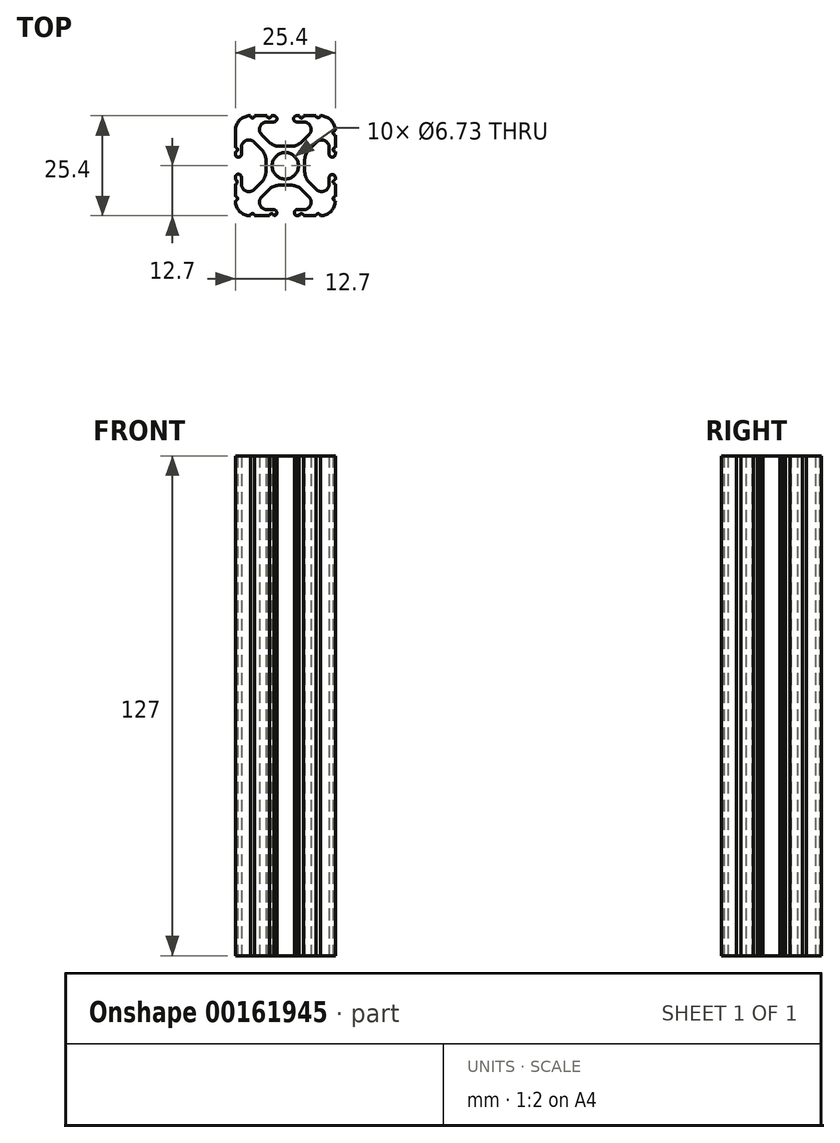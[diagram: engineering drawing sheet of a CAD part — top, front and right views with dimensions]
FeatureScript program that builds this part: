
annotation { "Feature Type Name" : "Feature", "Feature Type Description" : "" }
export const myFeature = defineFeature(function(context is Context, id is Id, definition is map)
    precondition{}
    {
        {
            var Q0;
            Q0=qCreatedBy(makeId("Top.planeOp"),FACE);
            var sketch = newSketch(context, id + "F0", { "sketchPlane" : qUnion([Q0])});
            skCircle(sketch, "E0", {"center": v(-12.7, 12.7) * mm, "radius": 3.36 * mm});
            skLineSegment(sketch, "E1.bottom", {"start": v(-11.24, 17.64) * mm, "end": v(-14.16, 17.64) * mm});
            skLineSegment(sketch, "E1.top", {"start": v(-11.24, 7.76) * mm, "end": v(-14.16, 7.76) * mm});
            skLineSegment(sketch, "E1.left", {"start": v(-7.76, 14.16) * mm, "end": v(-7.76, 11.24) * mm});
            skLineSegment(sketch, "E1.right", {"start": v(-17.64, 14.16) * mm, "end": v(-17.64, 11.24) * mm});
            skPoint(sketch, "E2.visualSharp", {"position": v(-25.4, 25.4) * mm});
            skPoint(sketch, "E3.visualSharp", {"position": v(0, 25.4) * mm});
            skPoint(sketch, "E4.visualSharp", {"position": v(0, 0) * mm});
            skPoint(sketch, "E5.visualSharp", {"position": v(-25.4, 0) * mm});
            skLineSegment(sketch, "E6.0", {"start": v(-18.7, 20.6) * mm, "end": v(-16.85, 18.76) * mm});
            skLineSegment(sketch, "E7.0", {"start": v(-20.6, 18.7) * mm, "end": v(-18.76, 16.85) * mm});
            skPoint(sketch, "E8.orphan", {"position": v(-23.85, 1.55) * mm});
            skPoint(sketch, "E9.orphan", {"position": v(-23.85, 23.85) * mm});
            skPoint(sketch, "E10.orphan", {"position": v(-1.55, 23.85) * mm});
            skPoint(sketch, "E11.orphan", {"position": v(-1.55, 1.55) * mm});
            skLineSegment(sketch, "E12", {"start": v(-8.55, 6.64) * mm, "end": v(-6.7, 4.8) * mm});
            skLineSegment(sketch, "E13.0", {"start": v(-18.7, 4.8) * mm, "end": v(-16.85, 6.64) * mm});
            skLineSegment(sketch, "E14.0", {"start": v(-20.6, 6.7) * mm, "end": v(-18.76, 8.55) * mm});
            skLineSegment(sketch, "E15.0", {"start": v(-8.55, 18.76) * mm, "end": v(-6.7, 20.6) * mm});
            skPoint(sketch, "E16.visualSharp", {"position": v(-23.85, 21.95) * mm});
            skArc(sketch, "E16.filletArc", {"start": v(-20.6, 18.7) * mm, "mid": v(-22.68, 19.1) * mm, "end": v(-23.85, 17.35) * mm});
            skPoint(sketch, "E17.visualSharp", {"position": v(-21.95, 23.85) * mm});
            skArc(sketch, "E17.filletArc", {"start": v(-17.35, 23.85) * mm, "mid": v(-19.1, 22.68) * mm, "end": v(-18.7, 20.6) * mm});
            skPoint(sketch, "E18.visualSharp", {"position": v(-5.34, 23.85) * mm});
            skLineSegment(sketch, "E19", {"start": v(-17.35, 23.85) * mm, "end": v(-15.58, 23.85) * mm});
            skLineSegment(sketch, "E20", {"start": v(-23.85, 17.35) * mm, "end": v(-23.85, 15.62) * mm});
            skLineSegment(sketch, "E21", {"start": v(-8.05, 1.55) * mm, "end": v(-9.78, 1.55) * mm});
            skArc(sketch, "E22.filletArc", {"start": v(-6.7, 20.6) * mm, "mid": v(-6.3, 22.68) * mm, "end": v(-8.05, 23.85) * mm});
            skPoint(sketch, "E23.visualSharp", {"position": v(-1.55, 3.45) * mm});
            skPoint(sketch, "E24.visualSharp", {"position": v(-3.45, 1.55) * mm});
            skArc(sketch, "E24.filletArc", {"start": v(-8.05, 1.55) * mm, "mid": v(-6.3, 2.73) * mm, "end": v(-6.7, 4.8) * mm});
            skArc(sketch, "E25.filletArc", {"start": v(-18.7, 4.8) * mm, "mid": v(-19.1, 2.73) * mm, "end": v(-17.35, 1.55) * mm});
            skArc(sketch, "E26.filletArc", {"start": v(-23.85, 8.05) * mm, "mid": v(-22.68, 6.3) * mm, "end": v(-20.6, 6.7) * mm});
            skLineSegment(sketch, "E27.bottom", {"start": v(-4.9, 0) * mm, "end": v(-8.05, 0) * mm});
            skLineSegment(sketch, "E27.top", {"start": v(-4.92, 25.4) * mm, "end": v(-8.05, 25.4) * mm});
            skLineSegment(sketch, "E27.left", {"start": v(0, 4.9) * mm, "end": v(0, 8.05) * mm});
            skLineSegment(sketch, "E27.right", {"start": v(-25.4, 4.9) * mm, "end": v(-25.4, 8.05) * mm});
            skArc(sketch, "E28.filletArc", {"start": v(-25.4, 3.81) * mm, "mid": v(-24.28, 1.12) * mm, "end": v(-21.59, 0) * mm});
            skArc(sketch, "E29.filletArc", {"start": v(-3.81, 0) * mm, "mid": v(-1.12, 1.12) * mm, "end": v(0, 3.8) * mm});
            skArc(sketch, "E30.filletArc", {"start": v(0, 21.59) * mm, "mid": v(-1.12, 24.28) * mm, "end": v(-3.8, 25.4) * mm});
            skArc(sketch, "E31.filletArc", {"start": v(-21.59, 25.4) * mm, "mid": v(-24.28, 24.28) * mm, "end": v(-25.4, 21.59) * mm});
            skPoint(sketch, "E32.newPointA", {"position": v(-17.64, 7.76) * mm});
            skArc(sketch, "E32.filletArc", {"start": v(-14.16, 7.76) * mm, "mid": v(-15.62, 7.47) * mm, "end": v(-16.85, 6.64) * mm});
            skPoint(sketch, "E33.newPointA", {"position": v(-7.76, 7.76) * mm});
            skArc(sketch, "E33.filletArc", {"start": v(-8.55, 6.64) * mm, "mid": v(-9.78, 7.47) * mm, "end": v(-11.24, 7.76) * mm});
            skArc(sketch, "E34.filletArc", {"start": v(-7.76, 11.24) * mm, "mid": v(-7.47, 9.78) * mm, "end": v(-6.64, 8.55) * mm});
            skArc(sketch, "E35.filletArc", {"start": v(-6.64, 16.85) * mm, "mid": v(-7.47, 15.62) * mm, "end": v(-7.76, 14.16) * mm});
            skPoint(sketch, "E36.newPointB", {"position": v(-7.76, 17.64) * mm});
            skArc(sketch, "E36.filletArc", {"start": v(-11.24, 17.64) * mm, "mid": v(-9.78, 17.93) * mm, "end": v(-8.55, 18.76) * mm});
            skPoint(sketch, "E37.newPointB", {"position": v(-17.64, 17.64) * mm});
            skArc(sketch, "E37.filletArc", {"start": v(-16.85, 18.76) * mm, "mid": v(-15.62, 17.93) * mm, "end": v(-14.16, 17.64) * mm});
            skArc(sketch, "E38.filletArc", {"start": v(-17.64, 14.16) * mm, "mid": v(-17.93, 15.62) * mm, "end": v(-18.76, 16.85) * mm});
            skArc(sketch, "E39.filletArc", {"start": v(-18.76, 8.55) * mm, "mid": v(-17.93, 9.78) * mm, "end": v(-17.64, 11.24) * mm});
            skLineSegment(sketch, "E40", {"start": v(-6.64, 8.55) * mm, "end": v(-4.8, 6.7) * mm});
            skPoint(sketch, "E41.visualSharp", {"position": v(-1.55, 21.95) * mm});
            skArc(sketch, "E42.filletArc", {"start": v(-4.8, 6.7) * mm, "mid": v(-2.73, 6.3) * mm, "end": v(-1.55, 8.05) * mm});
            skLineSegment(sketch, "E43", {"start": v(-1.55, 8.05) * mm, "end": v(-1.55, 9.78) * mm});
            skLineSegment(sketch, "E44", {"start": v(-6.64, 16.85) * mm, "end": v(-4.8, 18.7) * mm});
            skArc(sketch, "E45.filletArc", {"start": v(-1.55, 17.35) * mm, "mid": v(-2.73, 19.1) * mm, "end": v(-4.8, 18.7) * mm});
            skArc(sketch, "E46", {"start": v(-23.85, 9.78) * mm, "mid": v(-24.63, 10.56) * mm, "end": v(-25.4, 9.78) * mm});
            skArc(sketch, "E47", {"start": v(-25.4, 15.62) * mm, "mid": v(-24.63, 14.86) * mm, "end": v(-23.85, 15.62) * mm});
            skArc(sketch, "E48", {"start": v(-15.62, 23.85) * mm, "mid": v(-14.83, 24.63) * mm, "end": v(-15.62, 25.4) * mm});
            skArc(sketch, "E49", {"start": v(-9.78, 25.4) * mm, "mid": v(-10.6, 24.63) * mm, "end": v(-9.78, 23.85) * mm});
            skArc(sketch, "E50", {"start": v(-1.55, 15.62) * mm, "mid": v(-0.77, 14.88) * mm, "end": v(0, 15.62) * mm});
            skArc(sketch, "E51", {"start": v(0, 9.78) * mm, "mid": v(-0.77, 10.5) * mm, "end": v(-1.55, 9.78) * mm});
            skArc(sketch, "E52", {"start": v(-9.78, 1.55) * mm, "mid": v(-10.4, 0.77) * mm, "end": v(-9.78, 0) * mm});
            skArc(sketch, "E53", {"start": v(-15.62, 0) * mm, "mid": v(-14.85, 0.77) * mm, "end": v(-15.62, 1.55) * mm});
            skLineSegment(sketch, "E54.trimOffspring", {"start": v(-15.62, 1.55) * mm, "end": v(-17.35, 1.55) * mm});
            skLineSegment(sketch, "E55.trimOffspring", {"start": v(-16.7, 0) * mm, "end": v(-20.5, 0) * mm});
            skLineSegment(sketch, "E56.trimOffspring", {"start": v(-1.55, 15.62) * mm, "end": v(-1.55, 17.35) * mm});
            skLineSegment(sketch, "E57.trimOffspring", {"start": v(0, 15.62) * mm, "end": v(0, 16.26) * mm});
            skLineSegment(sketch, "E58.trimOffspring", {"start": v(-23.85, 9.78) * mm, "end": v(-23.85, 8.05) * mm});
            skLineSegment(sketch, "E59.trimOffspring", {"start": v(-25.4, 15.62) * mm, "end": v(-25.4, 16.26) * mm});
            skLineSegment(sketch, "E60.trimOffspring", {"start": v(-9.86, 23.85) * mm, "end": v(-8.05, 23.85) * mm});
            skLineSegment(sketch, "E61.trimOffspring", {"start": v(-15.58, 25.4) * mm, "end": v(-16.25, 25.4) * mm});
            skPoint(sketch, "E62.start.orphan", {"position": v(-15.62, 17.93) * mm});
            skPoint(sketch, "E63.start.orphan", {"position": v(-9.78, 17.93) * mm});
            skPoint(sketch, "E64.start.orphan", {"position": v(-7.47, 15.62) * mm});
            skPoint(sketch, "E65.start.orphan", {"position": v(-7.47, 9.78) * mm});
            skPoint(sketch, "E66.start.orphan", {"position": v(-17.93, 15.62) * mm});
            skPoint(sketch, "E67.start.orphan", {"position": v(-17.93, 9.78) * mm});
            skPoint(sketch, "E68.start.orphan", {"position": v(-9.78, 7.47) * mm});
            skPoint(sketch, "E69.start.orphan", {"position": v(-15.62, 7.47) * mm});
            skPoint(sketch, "E70.endSnap0", {"position": v(0, 18.6) * mm});
            skPoint(sketch, "E71.startSnap0", {"position": v(-1.55, 8.92) * mm});
            skArc(sketch, "E72", {"start": v(-4.92, 25.4) * mm, "mid": v(-4.37, 24.9) * mm, "end": v(-3.81, 25.4) * mm});
            skArc(sketch, "E73", {"start": v(-9.14, 25.4) * mm, "mid": v(-8.6, 24.86) * mm, "end": v(-8.05, 25.4) * mm});
            skArc(sketch, "E74", {"start": v(-17.35, 25.4) * mm, "mid": v(-16.8, 24.86) * mm, "end": v(-16.25, 25.4) * mm});
            skArc(sketch, "E75", {"start": v(-21.59, 25.4) * mm, "mid": v(-21.04, 24.85) * mm, "end": v(-20.49, 25.4) * mm});
            skLineSegment(sketch, "E76", {"start": v(-25.4, 21.59) * mm, "end": v(-25.4, 20.5) * mm});
            skArc(sketch, "E77", {"start": v(-25.4, 16.26) * mm, "mid": v(-24.84, 16.8) * mm, "end": v(-25.4, 17.35) * mm});
            skArc(sketch, "E78", {"start": v(-25.4, 8.05) * mm, "mid": v(-24.9, 8.6) * mm, "end": v(-25.4, 9.15) * mm});
            skArc(sketch, "E79", {"start": v(-25.4, 3.81) * mm, "mid": v(-24.85, 4.36) * mm, "end": v(-25.4, 4.9) * mm});
            skArc(sketch, "E80", {"start": v(-20.5, 0) * mm, "mid": v(-21.04, 0.55) * mm, "end": v(-21.59, 0) * mm});
            skArc(sketch, "E81", {"start": v(-15.62, 0) * mm, "mid": v(-16.16, 0.54) * mm, "end": v(-16.7, 0) * mm});
            skArc(sketch, "E82", {"start": v(-8.05, 0) * mm, "mid": v(-8.6, 0.55) * mm, "end": v(-9.15, 0) * mm});
            skArc(sketch, "E83", {"start": v(-3.81, 0) * mm, "mid": v(-4.35, 0.54) * mm, "end": v(-4.9, 0) * mm});
            skLineSegment(sketch, "E84.trimOffspring", {"start": v(-17.35, 25.4) * mm, "end": v(-20.49, 25.4) * mm});
            skLineSegment(sketch, "E85.trimOffspring", {"start": v(-25.4, 17.35) * mm, "end": v(-25.4, 21.59) * mm});
            skLineSegment(sketch, "E86.trimOffspring", {"start": v(-25.4, 9.15) * mm, "end": v(-25.4, 9.78) * mm});
            skLineSegment(sketch, "E87.trimOffspring", {"start": v(-9.15, 0) * mm, "end": v(-9.78, 0) * mm});
            skArc(sketch, "E88", {"start": v(0, 4.9) * mm, "mid": v(-0.54, 4.36) * mm, "end": v(0, 3.8) * mm});
            skArc(sketch, "E89", {"start": v(0, 9.15) * mm, "mid": v(-0.54, 8.6) * mm, "end": v(0, 8.05) * mm});
            skLineSegment(sketch, "E90.trimOffspring", {"start": v(0, 9.15) * mm, "end": v(0, 9.78) * mm});
            skArc(sketch, "E91", {"start": v(0, 21.59) * mm, "mid": v(-0.55, 21.04) * mm, "end": v(0, 20.5) * mm});
            skArc(sketch, "E92", {"start": v(0, 17.35) * mm, "mid": v(-0.55, 16.8) * mm, "end": v(0, 16.26) * mm});
            skLineSegment(sketch, "E93.trimOffspring", {"start": v(0, 17.35) * mm, "end": v(0, 20.5) * mm});
            skLineSegment(sketch, "E94.trimOffspring", {"start": v(-9.14, 25.4) * mm, "end": v(-9.86, 25.4) * mm});
            skSolve(sketch);
        }
        {
            var Q0;
            Q0=qSketchRegion(id+"F0",true);
            extrude(context, id + "F1", {"entities" : qUnion([Q0]), "depth" : 127 * mm});
        }
    });
